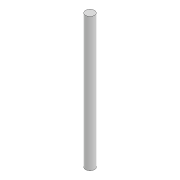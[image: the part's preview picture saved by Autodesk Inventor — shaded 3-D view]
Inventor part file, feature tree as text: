
AUTODESK INVENTOR PART (.ipt)
format: ipt  version: 2020 (Build 240168000, 168)  size: 70,656 bytes
history: native  units: mm
features: other x1, extrude x1, sketch x1
ambient origin geometry x8: Origin, YZ Plane, XZ Plane, XY Plane, X Axis, Y Axis, Z Axis, Center Point
bodies: Body1 (feature_tree)
feature tree (3):
  other  "Sólido1"
  extrude  "Extrusão1"  Depth=150.0mm TaperAngle=0.0deg
  sketch  "Esboço1"  dims[d0=10.0mm d1=150.0mm d2=0.0mm]
